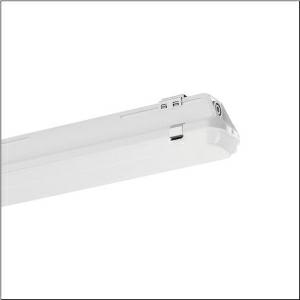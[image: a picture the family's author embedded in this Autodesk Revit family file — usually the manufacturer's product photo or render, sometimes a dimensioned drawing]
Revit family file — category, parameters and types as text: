
# Revit family: monsun_21_emergency_51fb107p487c3g
name_source: partatom
category: Lighting Fixtures
units: mm (PartAtom-declared; Revit-internal decimal feet)

## family parameters
Cut with Voids When Loaded = No
Host = Face
Light Source = No
Part Type = Normal
Room Calculation Point = No
Round Connector Dimension = Use Diameter
Shared = No

## types (1)
- --- (1 x LED, 820 lm, 7.1 W, 4000K)
    Apparent Load = 7 VA
    CIE Flux Codes = 47 77 93 94 100
    Color Rendering = 80
    Color Temperature = 4000K
    Default Elevation = 1800 mm
    Description = Monsun 21 emergency, damp-proof luminaire, chain hanger, primary optical cover: enclosure, of PMMA, light emission: direct distribution, primary light characteristic: symmetric, installation type: suspended mounting, surface-mounted, horizontal mounting, vertical mounting, LED, rated luminous flux: 8.090lm, luminous efficacy: 173lm/W, light colour: 840, colour temperature: 4000K, control gear: ON/OFF, with terminal, 4-pole, max. 2.5mm², mains connection: 220..240V, AC, 50/60Hz, rated input power: 51W, control gear: single battery element, battery: LiFePO4, 9Ah, housing, of glass-fibre reinforced polyester, uncoated, bright grey, incl. chain hanger, length: 1.590mm, width: 90mm, height: 88mm, clip for enclosure, of stainless steel (V2A), ceiling mounting element, of stainless steel (V2A), chain hanger, of stainless steel (V2A), protection rating (complete): IP66, insulation class (complete): insulation class I (protective earthing), certification: CE, UKCA, protection symbol: D, impact resistance: IK04, permissible operating ambient temperature: +5..+25°C, standard: EN 50419, EN 60598-2-1, EN 60598-2-22, corresponds to IFS (International Featured Standards) requirements for safety and quality in the food industry, for indoor or canopied outdoor use, no direct snow, no direct sun, no direct rain, LABS conformity tested according to VDMA 24364:2018-05, contact your sales advisor before using the luminaires in applications with unclear chemical exposure, large temperature fluctuations or condensation-forming humidity, packaging unit: 1 piece
    Height = 89 mm
    Lamp = 1 x LED
    Lamp Light Flux = 820 lm
    Lamp Power = 7.1 W
    Lamp count = 1
    Length = 1590 mm
    Luminous efficacy = 115 lm/W
    Manufacturer = Siteco
    ModVariant = No
    Model = 51FB107P487C3G
    Mounting Place = Ceiling
    Mounting Type = Surface mounted
    Number of Poles = 1
    OnlyDefault = Yes
    Power Factor = 1
    Product Name = Monsun 21 emergency
    Product group = damp-proof luminaire
    ProductGroupID = 300
    Protection Class = Protection class I
    Protection Degree = IP 66
    RLX_Detail_Level = 1
    RLX_Emergency_Light_Flux = 0 lm
    RLX_Emergency_Type = 0
    RLX_Emergency_Type_DB = No
    RlxData = <blob elided: 88969 chars, md5=4e57ad04>
    Socket = socket
    Standby Power = 0 W
    System Light Flux = 820 lm
    System Power = 7 W
    Type Comments = : emergency light operation: 3 h
    Type Image = l_1319656.jpg
    URL = http://relux.com
    VarID = @adj_038369
    Voltage = 0 V
    Weight = 0.00 kg
    Width = 90 mm

## geometry (parser evidence)
native form markers: Blend x4, Sweep x12
no freeform markers — native parametric forms only
